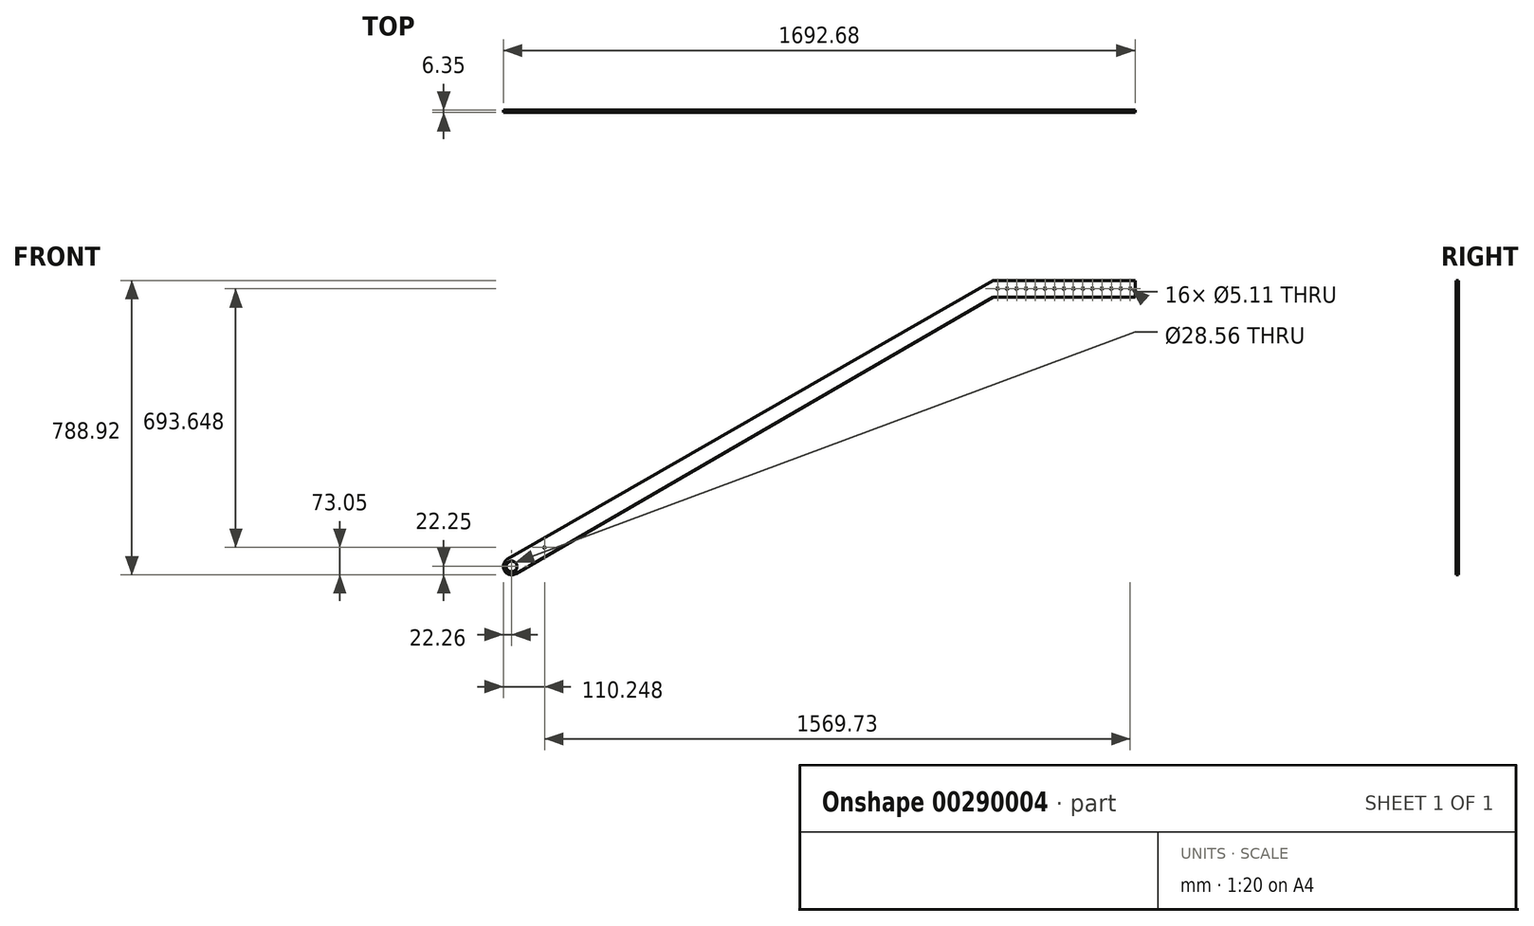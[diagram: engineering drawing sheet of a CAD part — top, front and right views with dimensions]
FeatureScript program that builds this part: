
annotation { "Feature Type Name" : "Feature", "Feature Type Description" : "" }
export const myFeature = defineFeature(function(context is Context, id is Id, definition is map)
    precondition{}
    {
        {
            var Q0;
            Q0=qCreatedBy(makeId("Front.planeOp"),FACE);
            var sketch = newSketch(context, id + "F0", { "sketchPlane" : qUnion([Q0])});
            skLineSegment(sketch, "E0", {"start": v(0, 0) * mm, "end": v(1289.42, 744.45) * mm, "construction": true});
            skLineSegment(sketch, "E1", {"start": v(1289.42, 744.45) * mm, "end": v(1670.42, 744.45) * mm, "construction": true});
            skCircle(sketch, "E2", {"center": v(0, 0) * mm, "radius": 14.28 * mm});
            skLineSegment(sketch, "E3", {"start": v(11.11, -19.25) * mm, "end": v(-11.11, 19.25) * mm, "construction": true});
            skArc(sketch, "E4", {"start": v(-11.11, 19.25) * mm, "mid": v(-19.29, -11.13) * mm, "end": v(11.11, -19.25) * mm});
            skLineSegment(sketch, "E5", {"start": v(-11.11, 19.25) * mm, "end": v(1289.42, 766.67) * mm});
            skLineSegment(sketch, "E6", {"start": v(1289.42, 766.67) * mm, "end": v(1670.42, 766.67) * mm});
            skLineSegment(sketch, "E7", {"start": v(1670.42, 766.67) * mm, "end": v(1670.42, 722.22) * mm});
            skLineSegment(sketch, "E8", {"start": v(1670.42, 722.22) * mm, "end": v(1289.42, 722.22) * mm});
            skLineSegment(sketch, "E9", {"start": v(1289.42, 722.22) * mm, "end": v(11.11, -19.25) * mm});
            skLineSegment(sketch, "E10", {"start": v(1289.42, 766.67) * mm, "end": v(1289.42, 722.22) * mm});
            skPoint(sketch, "E11", {"position": v(1289.42, 744.45) * mm});
            skPoint(sketch, "E12", {"position": v(1670.42, 744.45) * mm});
            skCircle(sketch, "E13", {"center": v(1302.12, 744.45) * mm, "radius": 2.55 * mm});
            skCircle(sketch, "E14.1.0.0", {"center": v(1327.52, 744.45) * mm, "radius": 2.55 * mm});
            skCircle(sketch, "E14.2.0.0", {"center": v(1352.92, 744.45) * mm, "radius": 2.55 * mm});
            skCircle(sketch, "E14.3.0.0", {"center": v(1378.32, 744.45) * mm, "radius": 2.55 * mm});
            skCircle(sketch, "E14.4.0.0", {"center": v(1403.72, 744.45) * mm, "radius": 2.55 * mm});
            skCircle(sketch, "E14.5.0.0", {"center": v(1429.12, 744.45) * mm, "radius": 2.55 * mm});
            skCircle(sketch, "E14.6.0.0", {"center": v(1454.52, 744.45) * mm, "radius": 2.55 * mm});
            skCircle(sketch, "E14.7.0.0", {"center": v(1479.92, 744.45) * mm, "radius": 2.55 * mm});
            skCircle(sketch, "E14.8.0.0", {"center": v(1505.32, 744.45) * mm, "radius": 2.55 * mm});
            skCircle(sketch, "E14.9.0.0", {"center": v(1530.72, 744.45) * mm, "radius": 2.55 * mm});
            skCircle(sketch, "E14.10.0.0", {"center": v(1556.12, 744.45) * mm, "radius": 2.55 * mm});
            skCircle(sketch, "E14.11.0.0", {"center": v(1581.52, 744.45) * mm, "radius": 2.55 * mm});
            skCircle(sketch, "E14.12.0.0", {"center": v(1606.92, 744.45) * mm, "radius": 2.55 * mm});
            skCircle(sketch, "E14.13.0.0", {"center": v(1632.32, 744.45) * mm, "radius": 2.55 * mm});
            skCircle(sketch, "E14.14.0.0", {"center": v(1657.72, 744.45) * mm, "radius": 2.55 * mm});
            skLineSegment(sketch, "E14.direction1", {"start": v(1302.12, 744.45) * mm, "end": v(1327.52, 744.45) * mm, "construction": true});
            skCircle(sketch, "E15", {"center": v(87.99, 50.8) * mm, "radius": 2.55 * mm});
            skSolve(sketch);
        }
        {
            var Q0;
            Q0 = qSketchRegion(id + "F0", true);
            extrude(context, id + "F1", {"entities" : qUnion([Q0]), "depth" : 6.35 * mm});
        }
    });
